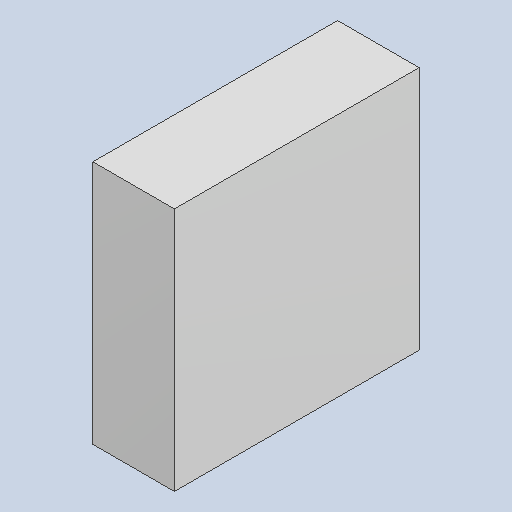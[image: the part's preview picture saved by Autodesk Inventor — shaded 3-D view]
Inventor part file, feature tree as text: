
AUTODESK INVENTOR PART (.ipt)
format: ipt  version: 2023.4 (Build 274418000, 418)  size: 81,408 bytes
history: native  units: mm
features: extrude x1
ambient origin geometry x8: Origin, YZ Plane, XZ Plane, XY Plane, X Axis, Y Axis, Z Axis, Center Point
bodies: Solid1 (feature_tree)
feature tree (1):
  extrude  "Extruded_15"  [1 undecoded]
note: 1 required parameter value undecoded (feature->parameter linkage not recoverable at this tier; creation-order binding heuristic only, values carry confidence <= 0.55)
